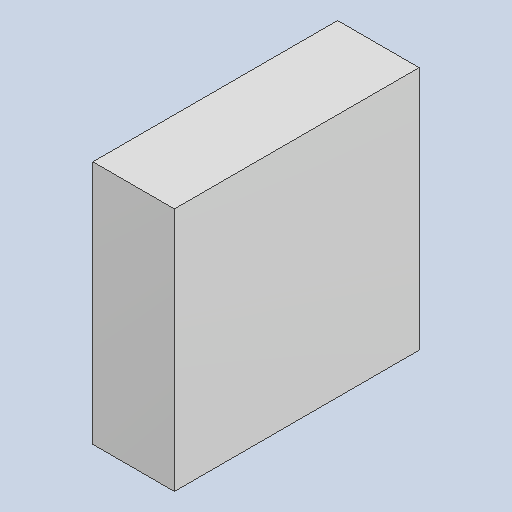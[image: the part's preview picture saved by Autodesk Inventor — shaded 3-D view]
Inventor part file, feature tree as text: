
AUTODESK INVENTOR PART (.ipt)
format: ipt  version: 2023.4 (Build 274418000, 418)  size: 81,408 bytes
history: native  units: mm
features: extrude x1
ambient origin geometry x8: Origin, YZ Plane, XZ Plane, XY Plane, X Axis, Y Axis, Z Axis, Center Point
bodies: Solid1 (feature_tree)
feature tree (1):
  extrude  "Extruded_32"  [1 undecoded]
note: 1 required parameter value undecoded (feature->parameter linkage not recoverable at this tier; creation-order binding heuristic only, values carry confidence <= 0.55)
